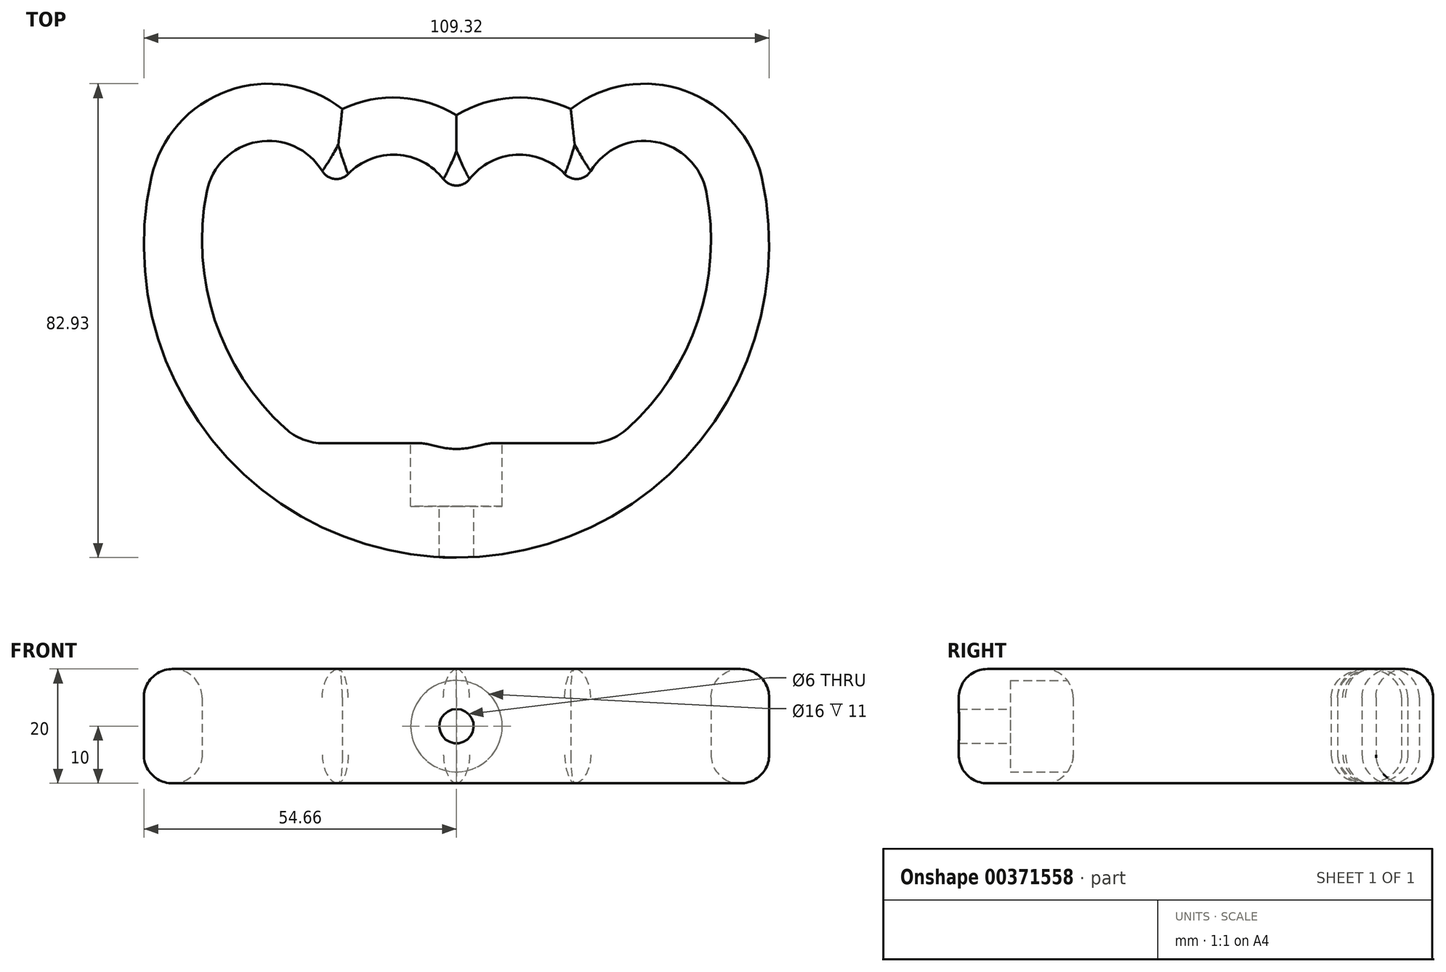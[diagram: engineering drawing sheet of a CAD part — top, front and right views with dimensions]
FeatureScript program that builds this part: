
annotation { "Feature Type Name" : "Feature", "Feature Type Description" : "" }
export const myFeature = defineFeature(function(context is Context, id is Id, definition is map)
    precondition{}
    {
        {
            var Q0;
            Q0=qCreatedBy(makeId("Top.planeOp"),FACE);
            var sketch = newSketch(context, id + "F0", { "sketchPlane" : qUnion([Q0])});
            skArc(sketch, "E0", {"start": v(-21.97, 1.21) * mm, "mid": v(-21.95, 1.36) * mm, "end": v(-21.93, 1.51) * mm});
            skArc(sketch, "E1", {"start": v(0, 0) * mm, "mid": v(0, 0.15) * mm, "end": v(0, 0.3) * mm});
            skArc(sketch, "E2", {"start": v(21.96, 1.2) * mm, "mid": v(21.95, 1.36) * mm, "end": v(21.93, 1.51) * mm});
            skArc(sketch, "E3", {"start": v(43.66, 4.82) * mm, "mid": v(34.8, 13.55) * mm, "end": v(23.47, 8.43) * mm});
            skArc(sketch, "E4", {"start": v(-136.1, 53.45) * mm, "mid": v(10.26, 0.26) * mm, "end": v(150.4, 68.16) * mm, "construction": true});
            skLineSegment(sketch, "E5", {"start": v(0, 0) * mm, "end": v(0, 199.92) * mm, "construction": true});
            skArc(sketch, "E6.0", {"start": v(53.37, 7.25) * mm, "mid": v(39.99, 22.48) * mm, "end": v(19.97, 19.3) * mm});
            skArc(sketch, "E7.0", {"start": v(31.93, 2.03) * mm, "mid": v(31.9, 2.3) * mm, "end": v(31.88, 2.56) * mm});
            skArc(sketch, "E8.0", {"start": v(10, -0.28) * mm, "mid": v(10, -0.01) * mm, "end": v(10, 0.25) * mm});
            skArc(sketch, "E9.0", {"start": v(-12.07, -0.16) * mm, "mid": v(-12.03, 0.1) * mm, "end": v(-12, 0.36) * mm});
            skArc(sketch, "E10.trimOffspring", {"start": v(-19.97, 19.3) * mm, "mid": v(-39.99, 22.48) * mm, "end": v(-53.37, 7.25) * mm});
            skArc(sketch, "E11.trimOffspring", {"start": v(-10, 0.25) * mm, "mid": v(-10, -0.01) * mm, "end": v(-10, -0.28) * mm});
            skArc(sketch, "E12.trimOffspring", {"start": v(0, 18.2) * mm, "mid": v(-9.84, 21.27) * mm, "end": v(-19.97, 19.3) * mm});
            skArc(sketch, "E13.trimOffspring", {"start": v(19.97, 19.3) * mm, "mid": v(9.84, 21.27) * mm, "end": v(0, 18.2) * mm});
            skArc(sketch, "E14.trimOffspring", {"start": v(-31.88, 2.56) * mm, "mid": v(-31.9, 2.3) * mm, "end": v(-31.93, 2.03) * mm});
            skArc(sketch, "E15", {"start": v(-43.66, 4.82) * mm, "mid": v(-42.22, -17.7) * mm, "end": v(-29.92, -36.6) * mm});
            skArc(sketch, "E16", {"start": v(53.37, 7.25) * mm, "mid": v(0, -59.2) * mm, "end": v(-53.37, 7.25) * mm});
            skArc(sketch, "E17.trimOffspring", {"start": v(-21.93, 1.51) * mm, "mid": v(-21.95, 1.36) * mm, "end": v(-21.96, 1.2) * mm});
            skArc(sketch, "E18.trimOffspring", {"start": v(-23.47, 8.43) * mm, "mid": v(-34.8, 13.55) * mm, "end": v(-43.66, 4.82) * mm});
            skArc(sketch, "E19.trimOffspring", {"start": v(-2.28, 7.01) * mm, "mid": v(-10.4, 11.29) * mm, "end": v(-18.93, 7.93) * mm});
            skArc(sketch, "E20.trimOffspring", {"start": v(0, 0.3) * mm, "mid": v(0, 0.15) * mm, "end": v(0, 0) * mm});
            skArc(sketch, "E21.trimOffspring", {"start": v(18.93, 7.93) * mm, "mid": v(10.4, 11.29) * mm, "end": v(2.28, 7.01) * mm});
            skArc(sketch, "E22.trimOffspring", {"start": v(21.93, 1.51) * mm, "mid": v(21.95, 1.36) * mm, "end": v(21.97, 1.21) * mm});
            skArc(sketch, "E23", {"start": v(-23.47, 8.43) * mm, "mid": v(-21.32, 7.06) * mm, "end": v(-18.93, 7.93) * mm});
            skArc(sketch, "E24", {"start": v(-2.28, 7.01) * mm, "mid": v(0, 5.89) * mm, "end": v(2.28, 7.01) * mm});
            skPoint(sketch, "E25.centerSnap0", {"position": v(21.2, 8.17) * mm});
            skArc(sketch, "E26", {"start": v(18.93, 7.93) * mm, "mid": v(21.32, 7.06) * mm, "end": v(23.47, 8.43) * mm});
            skLineSegment(sketch, "E27", {"start": v(0, 0) * mm, "end": v(0, -48.18) * mm, "construction": true});
            skLineSegment(sketch, "E28", {"start": v(-23.2, -39.2) * mm, "end": v(23.2, -39.2) * mm});
            skArc(sketch, "E29.trimOffspring", {"start": v(29.92, -36.6) * mm, "mid": v(42.22, -17.7) * mm, "end": v(43.66, 4.82) * mm});
            skPoint(sketch, "E30.visualSharp", {"position": v(-26.78, -39.2) * mm});
            skArc(sketch, "E30.filletArc", {"start": v(-29.92, -36.6) * mm, "mid": v(-26.8, -38.54) * mm, "end": v(-23.2, -39.2) * mm});
            skPoint(sketch, "E31.visualSharp", {"position": v(26.78, -39.2) * mm});
            skArc(sketch, "E31.filletArc", {"start": v(23.2, -39.2) * mm, "mid": v(26.8, -38.54) * mm, "end": v(29.92, -36.6) * mm});
            skSolve(sketch);
        }
        {
            var Q0;
            Q0=makeQuery(id+"F0.imprint","IMPRINT",FACE,{"disambiguationData":[TD([[makeQuery(id+"F0.imprint","IMPRINT",EDGE,{"derivedFrom":sQuery(id+"F0.wireOp",EDGE,"E6.0")}),1.0]])]});
            extrude(context, id + "F1", {"entities" : qUnion([Q0]), "endBound" : BoundingType.SYMMETRIC, "depth" : 20 * mm});
        }
        {
            var Q0;
            Q0=makeQuery(id+"F1.opExtrude","SWEPT_FACE",FACE,{"disambiguationData":[OSD([sQuery(id+"F0.wireOp",EDGE,"E28")])]});
            var sketch = newSketch(context, id + "F2", { "sketchPlane" : qUnion([Q0])});
            skPoint(sketch, "E32", {"position": v(0, 0) * mm});
            skSolve(sketch);
        }
        {
            var Q0;
            Q0=makeQuery(id+"F1.opExtrude","CAP_FACE",FACE,{"disambiguationData":[OSD([sQuery(id+"F0.wireOp",EDGE,"E3"),sQuery(id+"F0.wireOp",EDGE,"E6.0"),sQuery(id+"F0.wireOp",EDGE,"E10.trimOffspring"),sQuery(id+"F0.wireOp",EDGE,"E12.trimOffspring"),sQuery(id+"F0.wireOp",EDGE,"E13.trimOffspring"),sQuery(id+"F0.wireOp",EDGE,"E15"),sQuery(id+"F0.wireOp",EDGE,"E16"),sQuery(id+"F0.wireOp",EDGE,"E18.trimOffspring"),sQuery(id+"F0.wireOp",EDGE,"E19.trimOffspring"),sQuery(id+"F0.wireOp",EDGE,"E21.trimOffspring"),sQuery(id+"F0.wireOp",EDGE,"E23"),sQuery(id+"F0.wireOp",EDGE,"E24"),sQuery(id+"F0.wireOp",EDGE,"E26")])],"isStart":false});
            var Q1;
            Q1=makeQuery(id+"F1.opExtrude","CAP_FACE",FACE,{"disambiguationData":[OSD([sQuery(id+"F0.wireOp",EDGE,"E3"),sQuery(id+"F0.wireOp",EDGE,"E6.0"),sQuery(id+"F0.wireOp",EDGE,"E10.trimOffspring"),sQuery(id+"F0.wireOp",EDGE,"E12.trimOffspring"),sQuery(id+"F0.wireOp",EDGE,"E13.trimOffspring"),sQuery(id+"F0.wireOp",EDGE,"E15"),sQuery(id+"F0.wireOp",EDGE,"E16"),sQuery(id+"F0.wireOp",EDGE,"E18.trimOffspring"),sQuery(id+"F0.wireOp",EDGE,"E19.trimOffspring"),sQuery(id+"F0.wireOp",EDGE,"E21.trimOffspring"),sQuery(id+"F0.wireOp",EDGE,"E23"),sQuery(id+"F0.wireOp",EDGE,"E24"),sQuery(id+"F0.wireOp",EDGE,"E26")])],"isStart":true});
            fillet(context, id + "F3", {"entities" : qUnion([Q0, Q1]), "radius" : 5 * mm, "tangentPropagation" : true, "allowEdgeOverflow" : false});
        }
        {
            var Q0;
            Q0=sQuery(id+"F2.wireOp",VERTEX,"E32");
            var Q1;
            Q1=makeQuery(id+"F1.opExtrude","SWEPT_BODY",BODY,{"disambiguationData":[OSD([sQuery(id+"F0.wireOp",EDGE,"E3"),sQuery(id+"F0.wireOp",EDGE,"E6.0"),sQuery(id+"F0.wireOp",EDGE,"E10.trimOffspring"),sQuery(id+"F0.wireOp",EDGE,"E12.trimOffspring"),sQuery(id+"F0.wireOp",EDGE,"E13.trimOffspring"),sQuery(id+"F0.wireOp",EDGE,"E15"),sQuery(id+"F0.wireOp",EDGE,"E16"),sQuery(id+"F0.wireOp",EDGE,"E18.trimOffspring"),sQuery(id+"F0.wireOp",EDGE,"E19.trimOffspring"),sQuery(id+"F0.wireOp",EDGE,"E21.trimOffspring"),sQuery(id+"F0.wireOp",EDGE,"E23"),sQuery(id+"F0.wireOp",EDGE,"E24"),sQuery(id+"F0.wireOp",EDGE,"E26"),sQuery(id+"F0.wireOp",EDGE,"E28"),sQuery(id+"F0.wireOp",EDGE,"E29.trimOffspring")])]});
            hole(context, id + "F4", {"style" : HoleStyle.C_BORE, "endStyle" : HoleEndStyle.THROUGH, "holeDiameter" : 6 * mm, "cBoreDiameter" : 16 * mm, "cBoreDepth" : 10 * mm, "isTappedThrough" : true, "tappedDepth" : 12 * mm, "tapClearance" : 3, "locations" : qUnion([Q0]), "scope" : qUnion([Q1])});
        }
    });
